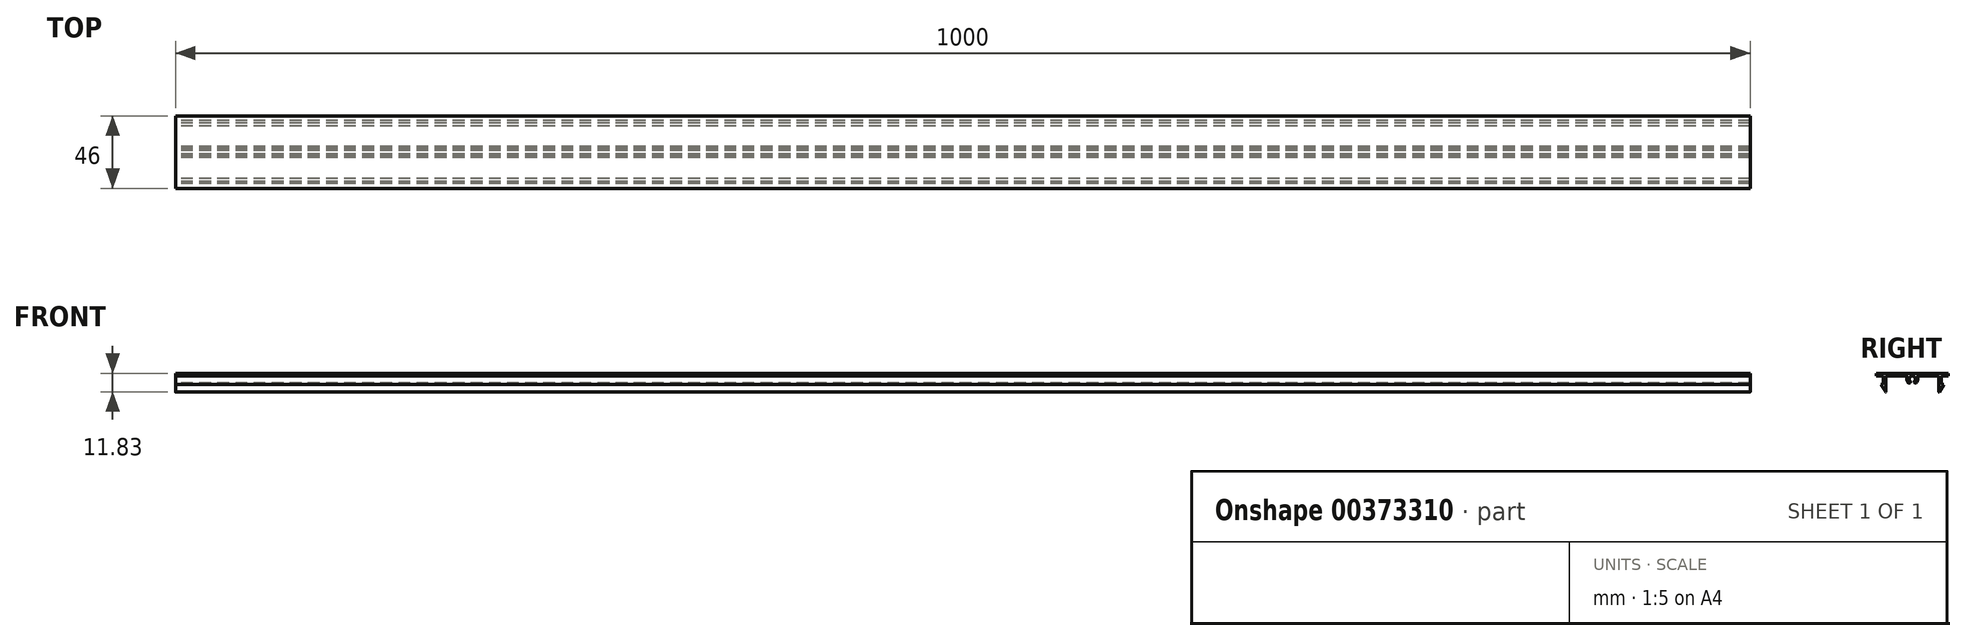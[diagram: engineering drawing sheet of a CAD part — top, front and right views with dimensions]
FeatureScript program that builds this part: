
annotation { "Feature Type Name" : "Feature", "Feature Type Description" : "" }
export const myFeature = defineFeature(function(context is Context, id is Id, definition is map)
    precondition{}
    {
        {
            var Q0;
            Q0=qCreatedBy(makeId("Right.planeOp"),FACE);
            var sketch = newSketch(context, id + "F0", { "sketchPlane" : qUnion([Q0])});
            skArc(sketch, "E0", {"start": v(24.4, -4.87) * mm, "mid": v(23, -1.68) * mm, "end": v(21.6, -4.87) * mm});
            skArc(sketch, "E1", {"start": v(25.57, -5.95) * mm, "mid": v(26.45, -4.18) * mm, "end": v(26.22, -2.22) * mm});
            skArc(sketch, "E2", {"start": v(24.4, -4.87) * mm, "mid": v(24.44, -6) * mm, "end": v(25.57, -5.95) * mm});
            skArc(sketch, "E3.MirrorC", {"start": v(21.6, -4.87) * mm, "mid": v(21.56, -6) * mm, "end": v(20.43, -5.95) * mm});
            skArc(sketch, "E4.trimOffspring", {"start": v(19.78, -2.22) * mm, "mid": v(19.55, -4.18) * mm, "end": v(20.43, -5.95) * mm});
            skLineSegment(sketch, "E5", {"start": v(0, 0) * mm, "end": v(0, -1.8) * mm});
            skLineSegment(sketch, "E6", {"start": v(0, 0) * mm, "end": v(46, 0) * mm});
            skLineSegment(sketch, "E7", {"start": v(46, 0) * mm, "end": v(46, -1.8) * mm});
            skLineSegment(sketch, "E8", {"start": v(46, -1.8) * mm, "end": v(41.5, -1.8) * mm});
            skLineSegment(sketch, "E9", {"start": v(0, -1.8) * mm, "end": v(4.5, -1.8) * mm});
            skLineSegment(sketch, "E10", {"start": v(23, 0) * mm, "end": v(23, -3.57) * mm, "construction": true});
            skLineSegment(sketch, "E11", {"start": v(4.5, -1.8) * mm, "end": v(4.5, -7) * mm});
            skLineSegment(sketch, "E12", {"start": v(4.5, -7) * mm, "end": v(2.95, -7) * mm});
            skLineSegment(sketch, "E13", {"start": v(6.3, -11.68) * mm, "end": v(6.3, -1.8) * mm});
            skArc(sketch, "E14", {"start": v(6.02, -11.76) * mm, "mid": v(6.2, -11.82) * mm, "end": v(6.3, -11.68) * mm});
            skPoint(sketch, "E14.second.point", {"position": v(6.05, -11.8) * mm});
            skPoint(sketch, "E14.third.point", {"position": v(6.33, -11.72) * mm});
            skPoint(sketch, "E14.third.point.positionSnap0", {"position": v(6.33, -12.23) * mm});
            skLineSegment(sketch, "E15.trimOffspring", {"start": v(6.02, -11.76) * mm, "end": v(2.95, -7) * mm});
            skPoint(sketch, "E16.start.orphan", {"position": v(9.7, -17.47) * mm});
            skPoint(sketch, "E17.orphan", {"position": v(6.3, -11.8) * mm});
            skLineSegment(sketch, "E18", {"start": v(6.3, -1.8) * mm, "end": v(19.5, -1.8) * mm});
            skPoint(sketch, "E19.visualSharp", {"position": v(19.99, -1.8) * mm});
            skArc(sketch, "E19.filletArc", {"start": v(19.78, -2.22) * mm, "mid": v(19.75, -1.93) * mm, "end": v(19.5, -1.8) * mm});
            skLineSegment(sketch, "E20.MirrorCS", {"start": v(39.7, -11.68) * mm, "end": v(39.7, -1.8) * mm});
            skArc(sketch, "E21.MirrorCS", {"start": v(39.98, -11.76) * mm, "mid": v(39.8, -11.82) * mm, "end": v(39.7, -11.68) * mm});
            skLineSegment(sketch, "E22.MirrorCS", {"start": v(39.98, -11.76) * mm, "end": v(43.05, -7) * mm});
            skLineSegment(sketch, "E23.MirrorCS", {"start": v(41.5, -1.8) * mm, "end": v(41.5, -7) * mm});
            skLineSegment(sketch, "E24.MirrorCS", {"start": v(41.5, -7) * mm, "end": v(43.05, -7) * mm});
            skLineSegment(sketch, "E25", {"start": v(39.7, -1.8) * mm, "end": v(26.5, -1.8) * mm});
            skPoint(sketch, "E26.visualSharp", {"position": v(26.01, -1.8) * mm});
            skArc(sketch, "E26.filletArc", {"start": v(26.5, -1.8) * mm, "mid": v(26.25, -1.93) * mm, "end": v(26.22, -2.22) * mm});
            skSolve(sketch);
        }
        {
            var Q0;
            Q0=makeQuery(id+"F0.imprint","IMPRINT",FACE,{"disambiguationData":[TD([[makeQuery(id+"F0.imprint","IMPRINT",EDGE,{"derivedFrom":sQuery(id+"F0.wireOp",EDGE,"E0")}),-1.0]])]});
            extrude(context, id + "F1", {"entities" : qUnion([Q0]), "depth" : 1000 * mm});
        }
    });
